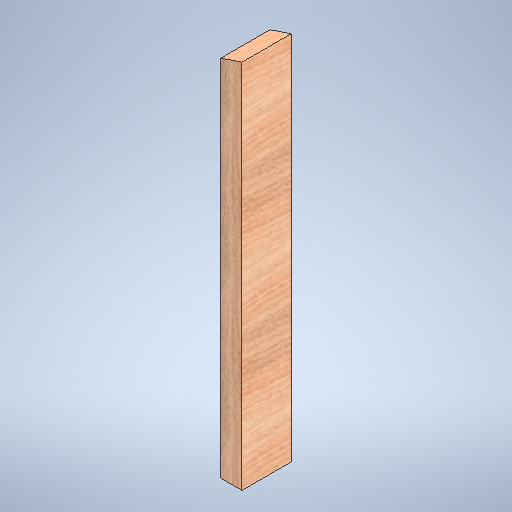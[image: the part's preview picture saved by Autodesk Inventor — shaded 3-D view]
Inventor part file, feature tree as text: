
AUTODESK INVENTOR PART (.ipt)
format: ipt  version: 2025.1 (Build 291241020, 241B)  size: 343,040 bytes
history: native  units: in
note: dims shown in document units (in); Inventor stores cm internally (conversion verified against a paired STEP export)
features: extrude x1, sketch x1
ambient origin geometry x8: Origin, YZ Plane, XZ Plane, XY Plane, X Axis, Y Axis, Z Axis, Center Point
bodies: Solid1 (feature_tree)
feature tree (2):
  extrude  "Extrusion1"  Depth=3.5in TaperAngle=0.0deg
  sketch  "Sketch1"  dims[d2=1.5in d3=3.5in d4=0.0in d5=25.901in d6=26.401in]
